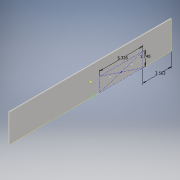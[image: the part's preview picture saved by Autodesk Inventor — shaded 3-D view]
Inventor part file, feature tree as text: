
AUTODESK INVENTOR PART (.ipt)
format: ipt  version: 2017 (Build 210142000, 142)  size: 109,568 bytes
history: native  units: in
note: dims shown in document units (in); Inventor stores cm internally (conversion verified against a paired STEP export)
features: sketch x3, extrude x1, hole x1
ambient origin geometry x8: Origin, YZ Plane, XZ Plane, XY Plane, X Axis, Y Axis, Z Axis, Center Point
bodies: Solid1 (feature_tree)
feature tree (5):
  extrude  "Extrusion1"  Depth=3.47in
  sketch  "Sketch2"  dims[d2=0.125in d3=0.0in d4=5.326in]
  hole  "Hole1"  [1 undecoded]
  sketch  "Sketch1"  dims[d0=20.0in d1=3.47in]
  sketch  "Sketch3"  dims[d5=1.74in d6=3.5625in d7=1.035in d8=1.332in d9=1.332in d10=0.177in d11=0.75in d12=0.409in d13=0.25in d14=90.0deg d15=1.0in d16=0.8108in]
note: 1 required parameter value undecoded (feature->parameter linkage not recoverable at this tier; creation-order binding heuristic only, values carry confidence <= 0.55)
